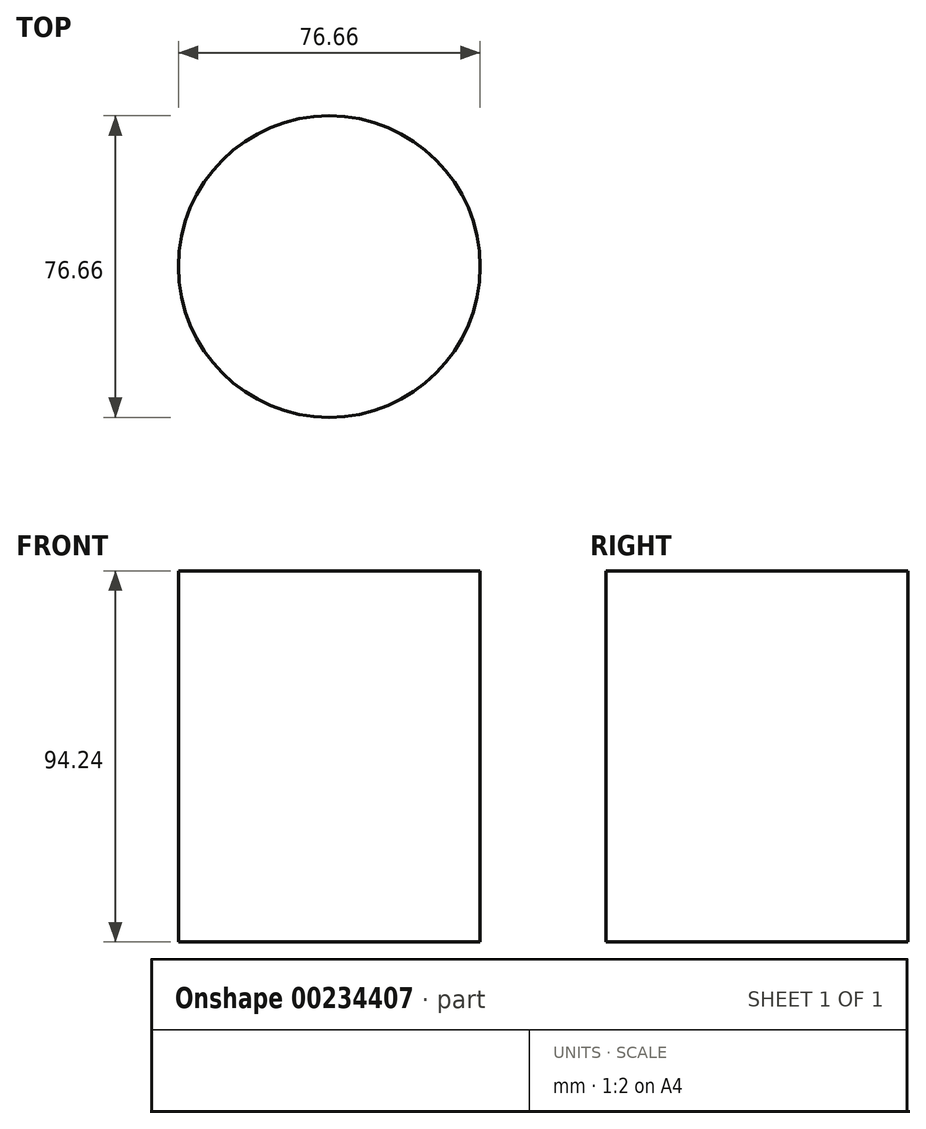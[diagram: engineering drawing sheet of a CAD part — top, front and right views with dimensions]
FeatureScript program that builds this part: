
annotation { "Feature Type Name" : "Feature", "Feature Type Description" : "" }
export const myFeature = defineFeature(function(context is Context, id is Id, definition is map)
    precondition{}
    {
        {
            var Q0;
            Q0=qCreatedBy(makeId("Top.planeOp"),FACE);
            var sketch = newSketch(context, id + "F1", { "sketchPlane" : qUnion([Q0])});
            skCircle(sketch, "E0", {"center": v(0, 0) * mm, "radius": 38.33 * mm});
            skSolve(sketch);
        }
        {
            var Q0;
            Q0=makeQuery(id+"F1.imprint","IMPRINT",FACE,{"disambiguationData":[TD([[makeQuery(id+"F1.imprint","IMPRINT",EDGE,{"derivedFrom":sQuery(id+"F1.wireOp",EDGE,"E0")}),1.0]])]});
            extrude(context, id + "F2", {"entities" : qUnion([Q0]), "depth" : 94.24 * mm});
        }
    });
